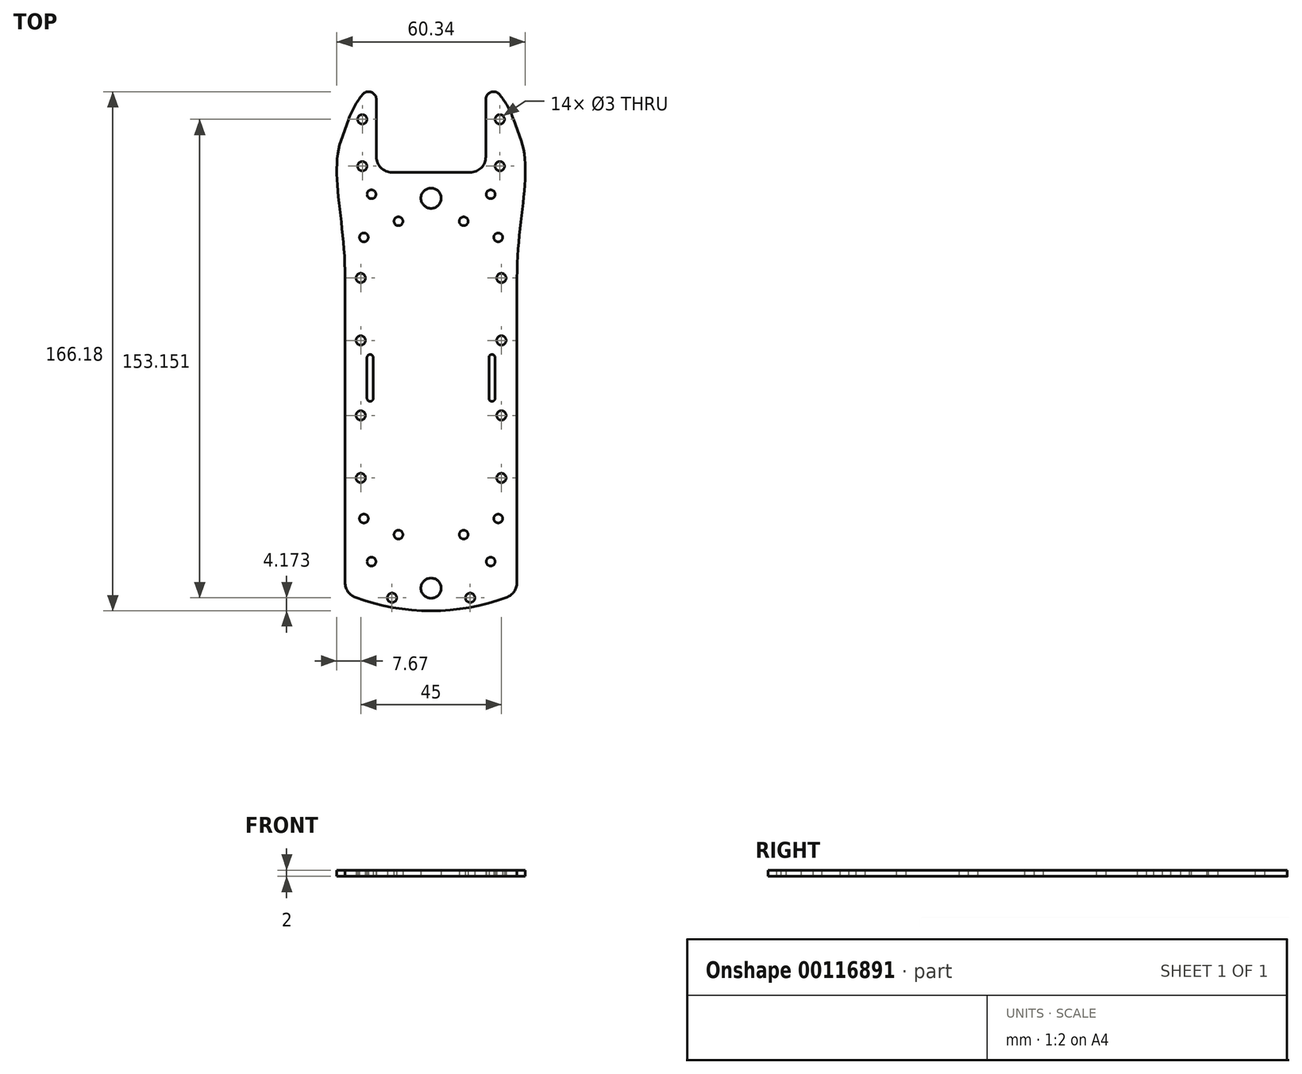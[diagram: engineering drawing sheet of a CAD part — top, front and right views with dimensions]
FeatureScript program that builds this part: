
annotation { "Feature Type Name" : "Feature", "Feature Type Description" : "" }
export const myFeature = defineFeature(function(context is Context, id is Id, definition is map)
    precondition{}
    {
        {
            var Q0;
            Q0=qCreatedBy(makeId("Top.planeOp"),FACE);
            var sketch = newSketch(context, id + "F0", { "sketchPlane" : qUnion([Q0])});
            skLineSegment(sketch, "E0", {"start": v(-27.15, 153.46) * mm, "end": v(-17.3, 155.2) * mm});
            skLineSegment(sketch, "E1", {"start": v(-17.3, 155.2) * mm, "end": v(-14.87, 141.4) * mm});
            skLineSegment(sketch, "E2", {"start": v(-14.87, 141.4) * mm, "end": v(-24.72, 139.67) * mm});
            skLineSegment(sketch, "E3", {"start": v(-24.72, 139.67) * mm, "end": v(-27.15, 153.46) * mm});
            skLineSegment(sketch, "E4", {"start": v(-8.87, 175.2) * mm, "end": v(-8.87, 29.62) * mm});
            skLineSegment(sketch, "E5", {"start": v(-63.87, 175.2) * mm, "end": v(-63.87, 29.62) * mm});
            skCircle(sketch, "E6", {"center": v(-51.37, 111.4) * mm, "radius": 1.5 * mm});
            skCircle(sketch, "E7", {"center": v(-21.37, 111.4) * mm, "radius": 1.5 * mm});
            skCircle(sketch, "E8", {"center": v(-51.37, 81.4) * mm, "radius": 1.5 * mm});
            skCircle(sketch, "E9", {"center": v(-21.37, 81.4) * mm, "radius": 1.5 * mm});
            skCircle(sketch, "E10", {"center": v(-17.3, 155.2) * mm, "radius": 1.43 * mm});
            skCircle(sketch, "E11", {"center": v(-27.15, 153.46) * mm, "radius": 1.43 * mm});
            skCircle(sketch, "E12", {"center": v(-24.72, 139.67) * mm, "radius": 1.43 * mm});
            skCircle(sketch, "E13", {"center": v(-14.87, 141.4) * mm, "radius": 1.43 * mm});
            skLineSegment(sketch, "E14", {"start": v(-63.87, 175.2) * mm, "end": v(-8.87, 175.2) * mm});
            skLineSegment(sketch, "E15", {"start": v(-45.6, 153.46) * mm, "end": v(-55.44, 155.2) * mm});
            skLineSegment(sketch, "E16", {"start": v(-55.44, 155.2) * mm, "end": v(-57.87, 141.4) * mm});
            skLineSegment(sketch, "E17", {"start": v(-57.87, 141.4) * mm, "end": v(-48.02, 139.67) * mm});
            skLineSegment(sketch, "E18", {"start": v(-48.02, 139.67) * mm, "end": v(-45.6, 153.46) * mm});
            skCircle(sketch, "E19", {"center": v(-55.44, 155.2) * mm, "radius": 1.43 * mm});
            skCircle(sketch, "E20", {"center": v(-45.6, 153.46) * mm, "radius": 1.43 * mm});
            skCircle(sketch, "E21", {"center": v(-48.02, 139.67) * mm, "radius": 1.43 * mm});
            skCircle(sketch, "E22", {"center": v(-57.87, 141.4) * mm, "radius": 1.43 * mm});
            skLineSegment(sketch, "E23", {"start": v(-63.87, 29.62) * mm, "end": v(-8.87, 29.62) * mm});
            skLineSegment(sketch, "E24.bottom", {"start": v(-54.37, 114.4) * mm, "end": v(-18.37, 114.4) * mm});
            skLineSegment(sketch, "E24.top", {"start": v(-54.37, 78.4) * mm, "end": v(-18.37, 78.4) * mm});
            skLineSegment(sketch, "E24.left", {"start": v(-54.37, 114.4) * mm, "end": v(-54.37, 78.4) * mm});
            skLineSegment(sketch, "E24.right", {"start": v(-18.37, 114.4) * mm, "end": v(-18.37, 78.4) * mm});
            skLineSegment(sketch, "E25", {"start": v(-57.87, 51.4) * mm, "end": v(-48.02, 53.14) * mm});
            skLineSegment(sketch, "E26", {"start": v(-48.02, 53.14) * mm, "end": v(-45.6, 39.36) * mm});
            skLineSegment(sketch, "E27", {"start": v(-45.6, 39.36) * mm, "end": v(-55.44, 37.62) * mm});
            skLineSegment(sketch, "E28", {"start": v(-55.44, 37.62) * mm, "end": v(-57.87, 51.4) * mm});
            skLineSegment(sketch, "E29", {"start": v(-24.72, 53.14) * mm, "end": v(-14.87, 51.4) * mm});
            skLineSegment(sketch, "E30", {"start": v(-14.87, 51.4) * mm, "end": v(-17.3, 37.62) * mm});
            skLineSegment(sketch, "E31", {"start": v(-17.3, 37.62) * mm, "end": v(-27.15, 39.36) * mm});
            skLineSegment(sketch, "E32", {"start": v(-27.15, 39.36) * mm, "end": v(-24.72, 53.14) * mm});
            skCircle(sketch, "E33", {"center": v(-57.87, 51.4) * mm, "radius": 1.43 * mm});
            skCircle(sketch, "E34", {"center": v(-48.02, 53.14) * mm, "radius": 1.43 * mm});
            skCircle(sketch, "E35", {"center": v(-45.6, 39.36) * mm, "radius": 1.43 * mm});
            skCircle(sketch, "E36", {"center": v(-55.44, 37.62) * mm, "radius": 1.43 * mm});
            skCircle(sketch, "E37", {"center": v(-27.15, 39.36) * mm, "radius": 1.43 * mm});
            skCircle(sketch, "E38", {"center": v(-24.72, 53.14) * mm, "radius": 1.43 * mm});
            skCircle(sketch, "E39", {"center": v(-14.87, 51.4) * mm, "radius": 1.43 * mm});
            skCircle(sketch, "E40", {"center": v(-17.3, 37.62) * mm, "radius": 1.43 * mm});
            skLineSegment(sketch, "E41", {"start": v(-36.37, 175.2) * mm, "end": v(-36.37, 125.26) * mm});
            skPoint(sketch, "E42", {"position": v(-36.37, 197.7) * mm});
            skArc(sketch, "E43", {"start": v(-8.87, 175.2) * mm, "mid": v(-36.37, 197.7) * mm, "end": v(-63.87, 175.2) * mm});
            skCircle(sketch, "E44", {"center": v(-36.37, 175.2) * mm, "radius": 1.5 * mm});
            skPoint(sketch, "E45.visualSharp", {"position": v(-63.87, 175.2) * mm});
            skPoint(sketch, "E46.visualSharp", {"position": v(-8.87, 175.2) * mm});
            skLineSegment(sketch, "E47", {"start": v(-54.15, 96.4) * mm, "end": v(-54.37, 96.4) * mm});
            skPoint(sketch, "E47.endSnap0", {"position": v(-54.37, 96.4) * mm});
            skArc(sketch, "E48", {"start": v(-60.6, 26.2) * mm, "mid": v(-36.37, 21.87) * mm, "end": v(-12.14, 26.2) * mm});
            skCircle(sketch, "E49", {"center": v(-58.87, 128.4) * mm, "radius": 1.5 * mm});
            skCircle(sketch, "E50", {"center": v(-58.87, 108.4) * mm, "radius": 1.5 * mm});
            skCircle(sketch, "E51", {"center": v(-58.87, 84.4) * mm, "radius": 1.5 * mm});
            skCircle(sketch, "E52", {"center": v(-58.87, 64.4) * mm, "radius": 1.5 * mm});
            skCircle(sketch, "E53.MirrorC", {"center": v(-13.87, 128.4) * mm, "radius": 1.5 * mm});
            skCircle(sketch, "E54.MirrorC", {"center": v(-13.87, 108.4) * mm, "radius": 1.5 * mm});
            skCircle(sketch, "E55.MirrorC", {"center": v(-13.87, 84.4) * mm, "radius": 1.5 * mm});
            skCircle(sketch, "E56.MirrorC", {"center": v(-13.87, 64.4) * mm, "radius": 1.5 * mm});
            skLineSegment(sketch, "E57", {"start": v(-63.87, 30.89) * mm, "end": v(-63.87, 29.62) * mm});
            skLineSegment(sketch, "E58", {"start": v(-8.87, 30.89) * mm, "end": v(-8.87, 29.62) * mm});
            skLineSegment(sketch, "E59", {"start": v(-48.87, 162.2) * mm, "end": v(-23.87, 162.2) * mm});
            skLineSegment(sketch, "E60", {"start": v(-53.87, 167.2) * mm, "end": v(-53.87, 191.57) * mm});
            skLineSegment(sketch, "E61", {"start": v(-18.87, 167.2) * mm, "end": v(-18.87, 191.57) * mm});
            skCircle(sketch, "E62", {"center": v(-56.37, 185.55) * mm, "radius": 2.5 * mm});
            skCircle(sketch, "E63", {"center": v(-16.37, 185.55) * mm, "radius": 2.5 * mm});
            skCircle(sketch, "E64", {"center": v(-58.37, 179.2) * mm, "radius": 1.5 * mm});
            skCircle(sketch, "E65", {"center": v(-14.37, 179.2) * mm, "radius": 1.5 * mm});
            skCircle(sketch, "E66", {"center": v(-55.87, 102.9) * mm, "radius": 1 * mm});
            skCircle(sketch, "E67", {"center": v(-55.87, 89.9) * mm, "radius": 1 * mm});
            skLineSegment(sketch, "E68", {"start": v(-56.87, 104.34) * mm, "end": v(-56.87, 88.08) * mm});
            skLineSegment(sketch, "E69", {"start": v(-54.87, 103.71) * mm, "end": v(-54.87, 88.49) * mm});
            skCircle(sketch, "E70.MirrorC", {"center": v(-16.87, 102.9) * mm, "radius": 1 * mm});
            skCircle(sketch, "E71.MirrorC", {"center": v(-16.87, 89.9) * mm, "radius": 1 * mm});
            skLineSegment(sketch, "E72.MirrorCS", {"start": v(-17.87, 103.71) * mm, "end": v(-17.87, 88.49) * mm});
            skLineSegment(sketch, "E73.MirrorCS", {"start": v(-15.87, 104.34) * mm, "end": v(-15.87, 88.08) * mm});
            skPoint(sketch, "E74.visualSharp", {"position": v(-53.87, 162.2) * mm});
            skArc(sketch, "E74.filletArc", {"start": v(-53.87, 167.2) * mm, "mid": v(-52.4, 163.66) * mm, "end": v(-48.87, 162.2) * mm});
            skPoint(sketch, "E75.visualSharp", {"position": v(-18.87, 162.2) * mm});
            skArc(sketch, "E75.filletArc", {"start": v(-23.87, 162.2) * mm, "mid": v(-20.33, 163.66) * mm, "end": v(-18.87, 167.2) * mm});
            skPoint(sketch, "E76.visualSharp", {"position": v(-63.87, 27.5) * mm});
            skArc(sketch, "E76.filletArc", {"start": v(-63.87, 30.89) * mm, "mid": v(-62.97, 28.03) * mm, "end": v(-60.6, 26.2) * mm});
            skPoint(sketch, "E77.visualSharp", {"position": v(-8.87, 27.5) * mm});
            skArc(sketch, "E77.filletArc", {"start": v(-12.14, 26.2) * mm, "mid": v(-9.77, 28.03) * mm, "end": v(-8.87, 30.89) * mm});
            skCircle(sketch, "E78", {"center": v(-36.37, 29.12) * mm, "radius": 3.25 * mm});
            skPoint(sketch, "E78.centerSnap0", {"position": v(-36.37, 29.62) * mm});
            skCircle(sketch, "E79", {"center": v(-48.87, 26.04) * mm, "radius": 1.5 * mm});
            skCircle(sketch, "E80", {"center": v(-23.87, 26.04) * mm, "radius": 1.5 * mm});
            skCircle(sketch, "E81", {"center": v(-36.37, 153.94) * mm, "radius": 3.25 * mm});
            skFitSpline(sketch, "E82", {"points": [v(-63.87, 175.2) * mm, v(-63.87, 128.4) * mm], "startDerivative": vector(-18, -30) * mm, "endDerivative": vector(0, -60) * mm});
            skPoint(sketch, "E83", {"position": v(-63.87, 96.4) * mm});
            skFitSpline(sketch, "E84.MirrorCS", {"points": [v(-8.87, 175.2) * mm, v(-8.87, 128.4) * mm], "startDerivative": vector(18, -30) * mm, "endDerivative": vector(0, -60) * mm});
            skLineSegment(sketch, "E85", {"start": v(-60.12, 186.51) * mm, "end": v(-70.05, 158.84) * mm});
            skLineSegment(sketch, "E86", {"start": v(-14.12, 190.7) * mm, "end": v(-3.8, 161.93) * mm});
            skCircle(sketch, "E87", {"center": v(-46.8, 146.56) * mm, "radius": 1.43 * mm});
            skCircle(sketch, "E88.MirrorC", {"center": v(-25.93, 146.56) * mm, "radius": 1.43 * mm});
            skLineSegment(sketch, "E89", {"start": v(-63.87, 96.4) * mm, "end": v(-81.19, 96.4) * mm});
            skCircle(sketch, "E90.MirrorC", {"center": v(-46.8, 46.25) * mm, "radius": 1.43 * mm});
            skCircle(sketch, "E91.MirrorC", {"center": v(-25.93, 46.25) * mm, "radius": 1.43 * mm});
            skCircle(sketch, "E92", {"center": v(-58.37, 164.2) * mm, "radius": 1.5 * mm});
            skCircle(sketch, "E93", {"center": v(-14.37, 164.2) * mm, "radius": 1.5 * mm});
            skSolve(sketch);
        }
        {
            var Q0;
            {var subQ46=sQuery(id+"F0.wireOp",EDGE,"E4");Q0=makeQuery(id+"F0.imprint","IMPRINT",FACE,{"disambiguationData":[TD([[makeQuery(id+"F0.imprint","IMPRINT",EDGE,{"derivedFrom":subQ46}),-1.0]])]});}
            var Q1;
            {var subQ3=sQuery(id+"F0.wireOp",EDGE,"E20");var subQ13=sQuery(id+"F0.wireOp",EDGE,"E15");var subQ14=makeQuery(id+"F0.imprint","INTERSECT",VERTEX,{"derivedFrom":[subQ13,subQ3]});Q1=makeQuery(id+"F0.imprint","IMPRINT",FACE,{"disambiguationData":[TD([[makeQuery(id+"F0.imprint","IMPRINT",EDGE,{"disambiguationData":[TD([[subQ14,-1.0]])],"derivedFrom":subQ13}),1.0]])]});}
            var Q2;
            {var subQ3=sQuery(id+"F0.wireOp",EDGE,"E11");var subQ10=sQuery(id+"F0.wireOp",EDGE,"E0");var subQ15=makeQuery(id+"F0.imprint","INTERSECT",VERTEX,{"derivedFrom":[subQ10,subQ3]});Q2=makeQuery(id+"F0.imprint","IMPRINT",FACE,{"disambiguationData":[TD([[makeQuery(id+"F0.imprint","IMPRINT",EDGE,{"disambiguationData":[TD([[subQ15,-1.0]])],"derivedFrom":subQ10}),-1.0]])]});}
            var Q3;
            Q3=makeQuery(id+"F0.imprint","IMPRINT",FACE,{"disambiguationData":[TD([[makeQuery(id+"F0.imprint","IMPRINT",EDGE,{"derivedFrom":sQuery(id+"F0.wireOp",EDGE,"E6")}),-1.0]])]});
            var Q4;
            {var subQ3=sQuery(id+"F0.wireOp",EDGE,"E33");var subQ13=sQuery(id+"F0.wireOp",EDGE,"E25");var subQ14=makeQuery(id+"F0.imprint","INTERSECT",VERTEX,{"derivedFrom":[subQ13,subQ3]});Q4=makeQuery(id+"F0.imprint","IMPRINT",FACE,{"disambiguationData":[TD([[makeQuery(id+"F0.imprint","IMPRINT",EDGE,{"disambiguationData":[TD([[subQ14,-1.0]])],"derivedFrom":subQ13}),-1.0]])]});}
            var Q5;
            {var subQ3=sQuery(id+"F0.wireOp",EDGE,"E38");var subQ5=sQuery(id+"F0.wireOp",EDGE,"E29");var subQ6=makeQuery(id+"F0.imprint","INTERSECT",VERTEX,{"derivedFrom":[subQ5,subQ3]});Q5=makeQuery(id+"F0.imprint","IMPRINT",FACE,{"disambiguationData":[TD([[makeQuery(id+"F0.imprint","IMPRINT",EDGE,{"disambiguationData":[TD([[subQ6,-1.0]])],"derivedFrom":subQ5}),-1.0]])]});}
            var Q6;
            Q6=makeQuery(id+"F0.imprint","IMPRINT",FACE,{"disambiguationData":[TD([[makeQuery(id+"F0.imprint","IMPRINT",EDGE,{"derivedFrom":sQuery(id+"F0.wireOp",EDGE,"E6")}),1.0]])]});
            var Q7;
            Q7=makeQuery(id+"F0.imprint","IMPRINT",FACE,{"disambiguationData":[TD([[makeQuery(id+"F0.imprint","IMPRINT",EDGE,{"derivedFrom":sQuery(id+"F0.wireOp",EDGE,"E7")}),1.0]])]});
            var Q8;
            Q8=makeQuery(id+"F0.imprint","IMPRINT",FACE,{"disambiguationData":[TD([[makeQuery(id+"F0.imprint","IMPRINT",EDGE,{"derivedFrom":sQuery(id+"F0.wireOp",EDGE,"E9")}),1.0]])]});
            var Q9;
            Q9=makeQuery(id+"F0.imprint","IMPRINT",FACE,{"disambiguationData":[TD([[makeQuery(id+"F0.imprint","IMPRINT",EDGE,{"derivedFrom":sQuery(id+"F0.wireOp",EDGE,"E8")}),1.0]])]});
            var Q10;
            {var subQ0=sQuery(id+"F0.wireOp",EDGE,"E18");var subQ1=sQuery(id+"F0.wireOp",EDGE,"E15");var subQ2=makeQuery(id+"F0.imprint","INTERSECT",VERTEX,{"derivedFrom":[subQ1,subQ0]});Q10=makeQuery(id+"F0.imprint","IMPRINT",FACE,{"disambiguationData":[TD([[makeQuery(id+"F0.imprint","IMPRINT",EDGE,{"disambiguationData":[TD([[subQ2,-1.0]])],"derivedFrom":subQ1}),-1.0]])]});}
            var Q11;
            {var subQ0=sQuery(id+"F0.wireOp",EDGE,"E18");var subQ1=sQuery(id+"F0.wireOp",EDGE,"E17");var subQ2=makeQuery(id+"F0.imprint","INTERSECT",VERTEX,{"derivedFrom":[subQ1,subQ0]});Q11=makeQuery(id+"F0.imprint","IMPRINT",FACE,{"disambiguationData":[TD([[makeQuery(id+"F0.imprint","IMPRINT",EDGE,{"disambiguationData":[TD([[subQ2,1.0]])],"derivedFrom":subQ1}),-1.0]])]});}
            var Q12;
            {var subQ0=sQuery(id+"F0.wireOp",EDGE,"E18");var subQ1=sQuery(id+"F0.wireOp",EDGE,"E15");var subQ2=makeQuery(id+"F0.imprint","INTERSECT",VERTEX,{"derivedFrom":[subQ1,subQ0]});Q12=makeQuery(id+"F0.imprint","IMPRINT",FACE,{"disambiguationData":[TD([[makeQuery(id+"F0.imprint","IMPRINT",EDGE,{"disambiguationData":[TD([[subQ2,-1.0]])],"derivedFrom":subQ1}),1.0]])]});}
            var Q13;
            {var subQ0=sQuery(id+"F0.wireOp",EDGE,"E18");var subQ1=sQuery(id+"F0.wireOp",EDGE,"E17");var subQ2=makeQuery(id+"F0.imprint","INTERSECT",VERTEX,{"derivedFrom":[subQ1,subQ0]});Q13=makeQuery(id+"F0.imprint","IMPRINT",FACE,{"disambiguationData":[TD([[makeQuery(id+"F0.imprint","IMPRINT",EDGE,{"disambiguationData":[TD([[subQ2,1.0]])],"derivedFrom":subQ1}),1.0]])]});}
            var Q14;
            {var subQ0=sQuery(id+"F0.wireOp",EDGE,"E3");var subQ1=sQuery(id+"F0.wireOp",EDGE,"E0");var subQ2=makeQuery(id+"F0.imprint","INTERSECT",VERTEX,{"derivedFrom":[subQ1,subQ0]});Q14=makeQuery(id+"F0.imprint","IMPRINT",FACE,{"disambiguationData":[TD([[makeQuery(id+"F0.imprint","IMPRINT",EDGE,{"disambiguationData":[TD([[subQ2,-1.0]])],"derivedFrom":subQ1}),1.0]])]});}
            var Q15;
            {var subQ0=sQuery(id+"F0.wireOp",EDGE,"E3");var subQ1=sQuery(id+"F0.wireOp",EDGE,"E2");var subQ2=makeQuery(id+"F0.imprint","INTERSECT",VERTEX,{"derivedFrom":[subQ1,subQ0]});Q15=makeQuery(id+"F0.imprint","IMPRINT",FACE,{"disambiguationData":[TD([[makeQuery(id+"F0.imprint","IMPRINT",EDGE,{"disambiguationData":[TD([[subQ2,1.0]])],"derivedFrom":subQ1}),1.0]])]});}
            var Q16;
            {var subQ0=sQuery(id+"F0.wireOp",EDGE,"E3");var subQ1=sQuery(id+"F0.wireOp",EDGE,"E2");var subQ2=makeQuery(id+"F0.imprint","INTERSECT",VERTEX,{"derivedFrom":[subQ1,subQ0]});Q16=makeQuery(id+"F0.imprint","IMPRINT",FACE,{"disambiguationData":[TD([[makeQuery(id+"F0.imprint","IMPRINT",EDGE,{"disambiguationData":[TD([[subQ2,1.0]])],"derivedFrom":subQ1}),-1.0]])]});}
            var Q17;
            {var subQ0=sQuery(id+"F0.wireOp",EDGE,"E3");var subQ1=sQuery(id+"F0.wireOp",EDGE,"E0");var subQ2=makeQuery(id+"F0.imprint","INTERSECT",VERTEX,{"derivedFrom":[subQ1,subQ0]});Q17=makeQuery(id+"F0.imprint","IMPRINT",FACE,{"disambiguationData":[TD([[makeQuery(id+"F0.imprint","IMPRINT",EDGE,{"disambiguationData":[TD([[subQ2,-1.0]])],"derivedFrom":subQ1}),-1.0]])]});}
            var Q18;
            {var subQ0=sQuery(id+"F0.wireOp",EDGE,"E32");var subQ1=sQuery(id+"F0.wireOp",EDGE,"E29");var subQ2=makeQuery(id+"F0.imprint","INTERSECT",VERTEX,{"derivedFrom":[subQ1,subQ0]});Q18=makeQuery(id+"F0.imprint","IMPRINT",FACE,{"disambiguationData":[TD([[makeQuery(id+"F0.imprint","IMPRINT",EDGE,{"disambiguationData":[TD([[subQ2,-1.0]])],"derivedFrom":subQ1}),1.0]])]});}
            var Q19;
            {var subQ0=sQuery(id+"F0.wireOp",EDGE,"E32");var subQ1=sQuery(id+"F0.wireOp",EDGE,"E29");var subQ2=makeQuery(id+"F0.imprint","INTERSECT",VERTEX,{"derivedFrom":[subQ1,subQ0]});Q19=makeQuery(id+"F0.imprint","IMPRINT",FACE,{"disambiguationData":[TD([[makeQuery(id+"F0.imprint","IMPRINT",EDGE,{"disambiguationData":[TD([[subQ2,-1.0]])],"derivedFrom":subQ1}),-1.0]])]});}
            var Q20;
            {var subQ0=sQuery(id+"F0.wireOp",EDGE,"E32");var subQ1=sQuery(id+"F0.wireOp",EDGE,"E31");var subQ2=makeQuery(id+"F0.imprint","INTERSECT",VERTEX,{"derivedFrom":[subQ1,subQ0]});Q20=makeQuery(id+"F0.imprint","IMPRINT",FACE,{"disambiguationData":[TD([[makeQuery(id+"F0.imprint","IMPRINT",EDGE,{"disambiguationData":[TD([[subQ2,1.0]])],"derivedFrom":subQ1}),1.0]])]});}
            var Q21;
            {var subQ0=sQuery(id+"F0.wireOp",EDGE,"E32");var subQ1=sQuery(id+"F0.wireOp",EDGE,"E31");var subQ2=makeQuery(id+"F0.imprint","INTERSECT",VERTEX,{"derivedFrom":[subQ1,subQ0]});Q21=makeQuery(id+"F0.imprint","IMPRINT",FACE,{"disambiguationData":[TD([[makeQuery(id+"F0.imprint","IMPRINT",EDGE,{"disambiguationData":[TD([[subQ2,1.0]])],"derivedFrom":subQ1}),-1.0]])]});}
            var Q22;
            {var subQ0=sQuery(id+"F0.wireOp",EDGE,"E26");var subQ1=sQuery(id+"F0.wireOp",EDGE,"E25");var subQ2=makeQuery(id+"F0.imprint","INTERSECT",VERTEX,{"derivedFrom":[subQ1,subQ0]});Q22=makeQuery(id+"F0.imprint","IMPRINT",FACE,{"disambiguationData":[TD([[makeQuery(id+"F0.imprint","IMPRINT",EDGE,{"disambiguationData":[TD([[subQ2,1.0]])],"derivedFrom":subQ1}),1.0]])]});}
            var Q23;
            {var subQ0=sQuery(id+"F0.wireOp",EDGE,"E26");var subQ1=sQuery(id+"F0.wireOp",EDGE,"E25");var subQ2=makeQuery(id+"F0.imprint","INTERSECT",VERTEX,{"derivedFrom":[subQ1,subQ0]});Q23=makeQuery(id+"F0.imprint","IMPRINT",FACE,{"disambiguationData":[TD([[makeQuery(id+"F0.imprint","IMPRINT",EDGE,{"disambiguationData":[TD([[subQ2,1.0]])],"derivedFrom":subQ1}),-1.0]])]});}
            var Q24;
            {var subQ0=sQuery(id+"F0.wireOp",EDGE,"E27");var subQ1=sQuery(id+"F0.wireOp",EDGE,"E26");var subQ2=makeQuery(id+"F0.imprint","INTERSECT",VERTEX,{"derivedFrom":[subQ1,subQ0]});Q24=makeQuery(id+"F0.imprint","IMPRINT",FACE,{"disambiguationData":[TD([[makeQuery(id+"F0.imprint","IMPRINT",EDGE,{"disambiguationData":[TD([[subQ2,1.0]])],"derivedFrom":subQ1}),1.0]])]});}
            var Q25;
            {var subQ0=sQuery(id+"F0.wireOp",EDGE,"E27");var subQ1=sQuery(id+"F0.wireOp",EDGE,"E26");var subQ2=makeQuery(id+"F0.imprint","INTERSECT",VERTEX,{"derivedFrom":[subQ1,subQ0]});Q25=makeQuery(id+"F0.imprint","IMPRINT",FACE,{"disambiguationData":[TD([[makeQuery(id+"F0.imprint","IMPRINT",EDGE,{"disambiguationData":[TD([[subQ2,1.0]])],"derivedFrom":subQ1}),-1.0]])]});}
            var Q26;
            {var subQ1=sQuery(id+"F0.wireOp",EDGE,"E14");var subQ3=sQuery(id+"F0.wireOp",EDGE,"E60");var subQ4=makeQuery(id+"F0.imprint","INTERSECT",VERTEX,{"derivedFrom":[subQ1,subQ3]});Q26=makeQuery(id+"F0.imprint","IMPRINT",FACE,{"disambiguationData":[TD([[makeQuery(id+"F0.imprint","IMPRINT",EDGE,{"disambiguationData":[TD([[subQ4,-1.0]])],"derivedFrom":subQ3}),1.0]])]});}
            var Q27;
            {var subQ0=sQuery(id+"F0.wireOp",EDGE,"E62");var subQ1=makeQuery(id+"F0.imprint","INTERSECT",VERTEX,{"derivedFrom":[sQuery(id+"F0.wireOp",EDGE,"E43"),subQ0]});Q27=makeQuery(id+"F0.imprint","IMPRINT",FACE,{"disambiguationData":[TD([[makeQuery(id+"F0.imprint","IMPRINT",EDGE,{"disambiguationData":[TD([[subQ1,1.0]])],"derivedFrom":subQ0}),1.0]])]});}
            var Q28;
            {var subQ1=sQuery(id+"F0.wireOp",EDGE,"E14");var subQ3=sQuery(id+"F0.wireOp",EDGE,"E61");var subQ4=makeQuery(id+"F0.imprint","INTERSECT",VERTEX,{"derivedFrom":[subQ1,subQ3]});Q28=makeQuery(id+"F0.imprint","IMPRINT",FACE,{"disambiguationData":[TD([[makeQuery(id+"F0.imprint","IMPRINT",EDGE,{"disambiguationData":[TD([[subQ4,-1.0]])],"derivedFrom":subQ3}),-1.0]])]});}
            var Q29;
            {var subQ0=sQuery(id+"F0.wireOp",EDGE,"E63");var subQ1=makeQuery(id+"F0.imprint","INTERSECT",VERTEX,{"derivedFrom":[sQuery(id+"F0.wireOp",EDGE,"E43"),subQ0]});Q29=makeQuery(id+"F0.imprint","IMPRINT",FACE,{"disambiguationData":[TD([[makeQuery(id+"F0.imprint","IMPRINT",EDGE,{"disambiguationData":[TD([[subQ1,-1.0]])],"derivedFrom":subQ0}),1.0]])]});}
            var Q30;
            {var subQ1=sQuery(id+"F0.wireOp",EDGE,"E48");Q30=makeQuery(id+"F0.imprint","IMPRINT",FACE,{"disambiguationData":[TD([[makeQuery(id+"F0.imprint","IMPRINT",EDGE,{"derivedFrom":subQ1}),1.0]])]});}
            var Q31;
            {var subQ0=sQuery(id+"F0.wireOp",EDGE,"E82");Q31=makeQuery(id+"F0.imprint","IMPRINT",FACE,{"disambiguationData":[TD([[makeQuery(id+"F0.imprint","IMPRINT",EDGE,{"derivedFrom":subQ0}),1.0]])]});}
            var Q32;
            {var subQ0=sQuery(id+"F0.wireOp",EDGE,"E84.MirrorCS");Q32=makeQuery(id+"F0.imprint","IMPRINT",FACE,{"disambiguationData":[TD([[makeQuery(id+"F0.imprint","IMPRINT",EDGE,{"derivedFrom":subQ0}),-1.0]])]});}
            var Q33;
            {var subQ1=sQuery(id+"F0.wireOp",EDGE,"E43");var subQ3=sQuery(id+"F0.wireOp",EDGE,"E85");var subQ4=makeQuery(id+"F0.imprint","INTERSECT",VERTEX,{"derivedFrom":[subQ1,subQ3]});Q33=makeQuery(id+"F0.imprint","IMPRINT",FACE,{"disambiguationData":[TD([[makeQuery(id+"F0.imprint","IMPRINT",EDGE,{"disambiguationData":[TD([[subQ4,-1.0]])],"derivedFrom":subQ3}),1.0]])]});}
            var Q34;
            {var subQ1=sQuery(id+"F0.wireOp",EDGE,"E43");var subQ3=sQuery(id+"F0.wireOp",EDGE,"E86");var subQ4=makeQuery(id+"F0.imprint","INTERSECT",VERTEX,{"derivedFrom":[subQ1,subQ3]});Q34=makeQuery(id+"F0.imprint","IMPRINT",FACE,{"disambiguationData":[TD([[makeQuery(id+"F0.imprint","IMPRINT",EDGE,{"disambiguationData":[TD([[subQ4,-1.0]])],"derivedFrom":subQ3}),-1.0]])]});}
            extrude(context, id + "F1", {"entities" : qUnion([Q0, Q1, Q2, Q3, Q4, Q5, Q6, Q7, Q8, Q9, Q10, Q11, Q12, Q13, Q14, Q15, Q16, Q17, Q18, Q19, Q20, Q21, Q22, Q23, Q24, Q25, Q26, Q27, Q28, Q29, Q30, Q31, Q32, Q33, Q34]), "depth" : 2 * mm});
        }
    });
